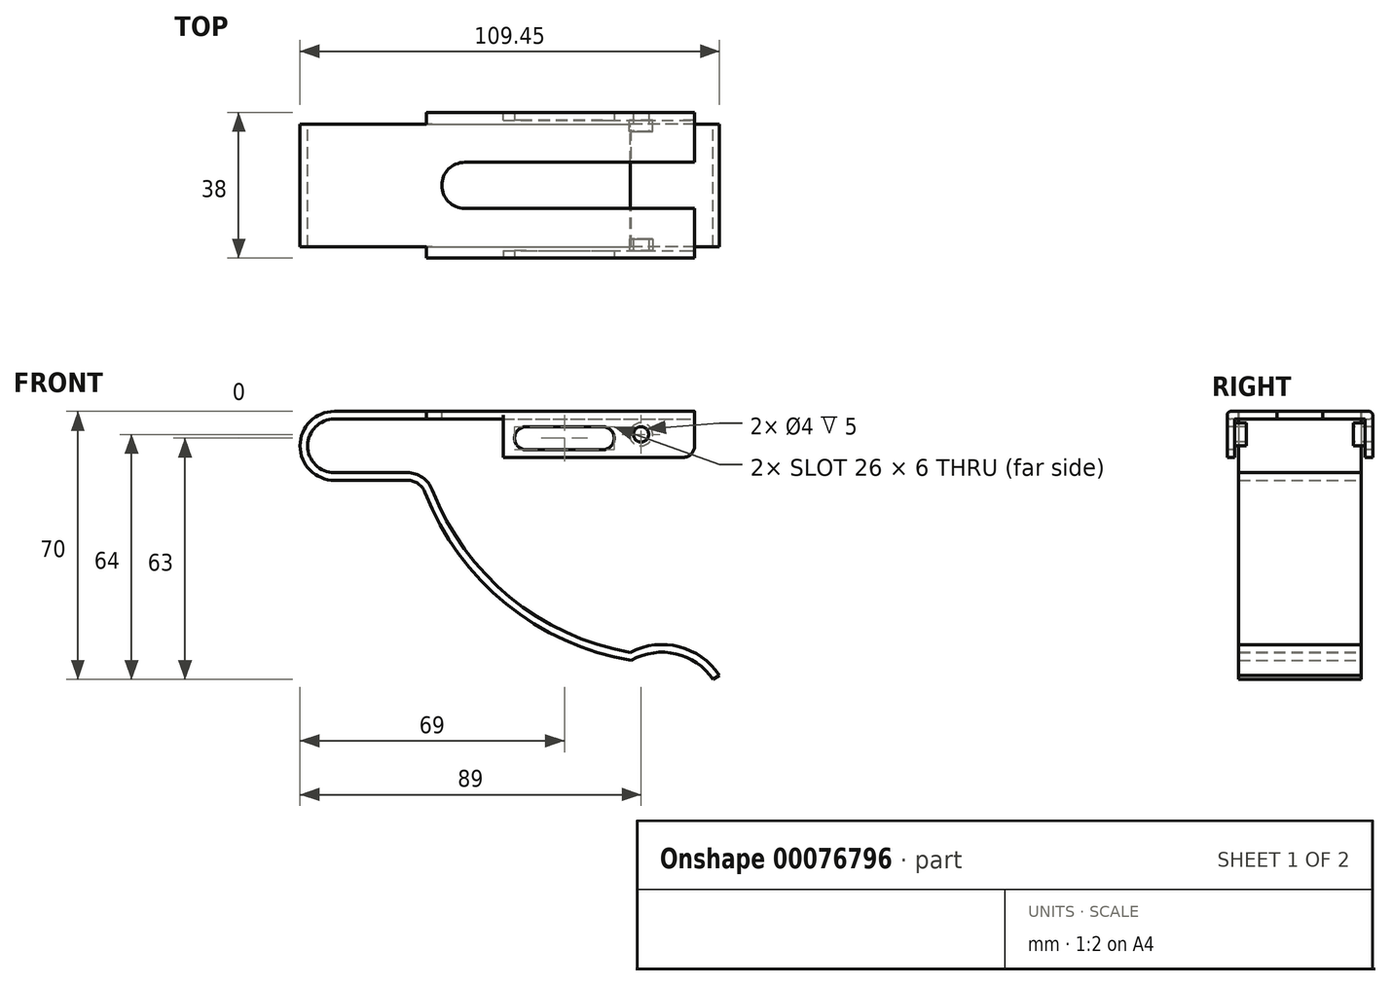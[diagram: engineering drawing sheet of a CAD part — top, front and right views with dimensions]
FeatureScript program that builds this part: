
annotation { "Feature Type Name" : "Feature", "Feature Type Description" : "" }
export const myFeature = defineFeature(function(context is Context, id is Id, definition is map)
    precondition{}
    {
        {
            var Q0;
            Q0=qCreatedBy(makeId("Front.planeOp"),FACE);
            var sketch = newSketch(context, id + "F0", { "sketchPlane" : qUnion([Q0])});
            skArc(sketch, "E0", {"start": v(0, 9) * mm, "mid": v(-9, 0) * mm, "end": v(0, -9) * mm});
            skLineSegment(sketch, "E1", {"start": v(0, 9) * mm, "end": v(94, 9) * mm});
            skLineSegment(sketch, "E2", {"start": v(0, -9) * mm, "end": v(19, -9) * mm});
            skArc(sketch, "E3", {"start": v(23.66, -12.2) * mm, "mid": v(44.77, -41.24) * mm, "end": v(77.5, -56) * mm});
            skArc(sketch, "E4", {"start": v(98.78, -61) * mm, "mid": v(89.13, -54.3) * mm, "end": v(77.5, -56) * mm});
            skPoint(sketch, "E5.visualSharp", {"position": v(22.52, -9) * mm});
            skArc(sketch, "E5.filletArc", {"start": v(23.66, -12.2) * mm, "mid": v(21.83, -9.88) * mm, "end": v(19, -9) * mm});
            skLineSegment(sketch, "E6.0", {"start": v(0, 7) * mm, "end": v(94, 7) * mm});
            skArc(sketch, "E6.1", {"start": v(0, 7) * mm, "mid": v(-7, 0) * mm, "end": v(0, -7) * mm});
            skArc(sketch, "E6.2", {"start": v(100.45, -59.9) * mm, "mid": v(89.94, -52.44) * mm, "end": v(77.15, -53.91) * mm});
            skArc(sketch, "E6.3", {"start": v(25.53, -11.47) * mm, "mid": v(45.77, -39.47) * mm, "end": v(77.15, -53.91) * mm});
            skArc(sketch, "E6.4", {"start": v(25.53, -11.47) * mm, "mid": v(22.96, -8.23) * mm, "end": v(19, -7) * mm});
            skLineSegment(sketch, "E6.5", {"start": v(0, -7) * mm, "end": v(19, -7) * mm});
            skLineSegment(sketch, "E7", {"start": v(94, 9) * mm, "end": v(94, 7) * mm});
            skLineSegment(sketch, "E8", {"start": v(100.45, -59.9) * mm, "end": v(98.78, -61) * mm});
            skSolve(sketch);
        }
        {
            var Q0;
            Q0 = qSketchRegion(id + "F0", true);
            extrude(context, id + "F1", {"entities" : qUnion([Q0]), "depth" : 16 * mm});
        }
        {
            var Q0;
            Q0=makeQuery(id+"F1.opExtrude","SWEPT_FACE",FACE,{"disambiguationData":[OSD([sQuery(id+"F0.wireOp",EDGE,"E1")])]});
            var sketch = newSketch(context, id + "F2", { "sketchPlane" : qUnion([Q0])});
            skLineSegment(sketch, "E9.bottom", {"start": v(79.88, -16) * mm, "end": v(24, -16) * mm});
            skLineSegment(sketch, "E9.top", {"start": v(94, -19) * mm, "end": v(24, -19) * mm});
            skLineSegment(sketch, "E9.left", {"start": v(94, -16) * mm, "end": v(94, -19) * mm});
            skLineSegment(sketch, "E9.right", {"start": v(24, -16) * mm, "end": v(24, -19) * mm});
            skLineSegment(sketch, "E10.top", {"start": v(94, -10.87) * mm, "end": v(79.88, -10.87) * mm});
            skLineSegment(sketch, "E10.left", {"start": v(94, -16) * mm, "end": v(94, -10.87) * mm});
            skLineSegment(sketch, "E10.right", {"start": v(79.88, -16) * mm, "end": v(79.88, -10.87) * mm});
            skSolve(sketch);
        }
        {
            var Q0;
            Q0=makeQuery(id+"F2.imprint","IMPRINT",FACE,{"disambiguationData":[TD([[makeQuery(id+"F2.imprint","IMPRINT",EDGE,{"derivedFrom":sQuery(id+"F2.wireOp",EDGE,"E10.top")}),1.0]])]});
            var Q1;
            {var subQ1=sQuery(id+"F2.wireOp",EDGE,"E9.bottom");Q1=makeQuery(id+"F2.imprint","IMPRINT",FACE,{"disambiguationData":[TD([[makeQuery(id+"F2.imprint","IMPRINT",EDGE,{"derivedFrom":subQ1}),-1.0]])]});}
            extrude(context, id + "F3", {"entities" : qUnion([Q0, Q1]), "operationType" : NewBodyOperationType.ADD, "oppositeDirection" : true, "depth" : 2 * mm});
        }
        {
            var Q0;
            Q0=makeQuery(id+"F3.opExtrude","SWEPT_FACE",FACE,{"disambiguationData":[OSD([sQuery(id+"F2.wireOp",EDGE,"E9.top")])]});
            var sketch = newSketch(context, id + "F4", { "sketchPlane" : qUnion([Q0])});
            skPoint(sketch, "E11", {"position": v(94, -3) * mm});
            skPoint(sketch, "E11.positionSnap0", {"position": v(94, 8) * mm});
            skPoint(sketch, "E12", {"position": v(94, 9) * mm});
            skLineSegment(sketch, "E13.bottom", {"start": v(44, 9) * mm, "end": v(94, 9) * mm});
            skLineSegment(sketch, "E13.top", {"start": v(44, -3) * mm, "end": v(94, -3) * mm});
            skLineSegment(sketch, "E13.left", {"start": v(44, 9) * mm, "end": v(44, -3) * mm});
            skLineSegment(sketch, "E13.right", {"start": v(94, 9) * mm, "end": v(94, -3) * mm});
            skSolve(sketch);
        }
        {
            var Q0;
            Q0 = qSketchRegion(id + "F4", true);
            extrude(context, id + "F5", {"entities" : qUnion([Q0]), "operationType" : NewBodyOperationType.ADD, "oppositeDirection" : true, "depth" : 2 * mm});
        }
        {
            var Q0;
            Q0=makeQuery(id+"F3.opExtrude","CAP_EDGE",EDGE,{"disambiguationData":[OSD([sQuery(id+"F2.wireOp",EDGE,"E9.top")])],"isStart":true});
            var Q1;
            Q1=makeQuery(id+"F3.opExtrude","CAP_EDGE",EDGE,{"disambiguationData":[OSD([sQuery(id+"F2.wireOp",EDGE,"E9.top")])],"isStart":false});
            fillet(context, id + "F6", {"entities" : qUnion([Q0, Q1]), "radius" : 1 * mm, "tangentPropagation" : true, "allowEdgeOverflow" : false});
        }
        {
            var Q0;
            Q0=makeQuery(id+"F1.opExtrude","SWEPT_BODY",BODY,{"disambiguationData":[OSD([sQuery(id+"F0.wireOp",EDGE,"E0"),sQuery(id+"F0.wireOp",EDGE,"E1"),sQuery(id+"F0.wireOp",EDGE,"E2"),sQuery(id+"F0.wireOp",EDGE,"E3"),sQuery(id+"F0.wireOp",EDGE,"E4"),sQuery(id+"F0.wireOp",EDGE,"E5.filletArc"),sQuery(id+"F0.wireOp",EDGE,"E6.0"),sQuery(id+"F0.wireOp",EDGE,"E6.1"),sQuery(id+"F0.wireOp",EDGE,"E6.2"),sQuery(id+"F0.wireOp",EDGE,"E6.3"),sQuery(id+"F0.wireOp",EDGE,"E6.4"),sQuery(id+"F0.wireOp",EDGE,"E6.5"),sQuery(id+"F0.wireOp",EDGE,"E7"),sQuery(id+"F0.wireOp",EDGE,"E8")])]});
            var Q1;
            Q1=qCreatedBy(makeId("Front.planeOp"),FACE);
            mirror(context, id + "F7", {"operationType" : NewBodyOperationType.ADD, "entities" : qUnion([Q0]), "mirrorPlane" : qUnion([Q1])});
        }
        {
            var Q0;
            {var subQ0=makeQuery(id+"F3.boolean.opBoolean","MERGE",FACE,{"derivedFrom":[makeQuery(id+"F1.opExtrude","SWEPT_FACE",FACE,{"disambiguationData":[OSD([sQuery(id+"F0.wireOp",EDGE,"E1")])]}),makeQuery(id+"F3.opExtrude","CAP_FACE",FACE,{"disambiguationData":[OSD([sQuery(id+"F2.wireOp",EDGE,"E9.bottom"),sQuery(id+"F2.wireOp",EDGE,"E9.top"),sQuery(id+"F2.wireOp",EDGE,"E9.left"),sQuery(id+"F2.wireOp",EDGE,"E9.right"),sQuery(id+"F2.wireOp",EDGE,"E10.top"),sQuery(id+"F2.wireOp",EDGE,"E10.left"),sQuery(id+"F2.wireOp",EDGE,"E10.right")])],"isStart":true})]});Q0=makeQuery(id+"F7.boolean.opBoolean","MERGE",FACE,{"derivedFrom":[subQ0,makeQuery(id+"F7.opPattern","COPY",FACE,{"derivedFrom":subQ0,"instanceName":"1"})]});}
            var sketch = newSketch(context, id + "F8", { "sketchPlane" : qUnion([Q0])});
            skPoint(sketch, "E14", {"position": v(0, 0) * mm});
            skArc(sketch, "E15", {"start": v(34, 6) * mm, "mid": v(28, 0) * mm, "end": v(34, -6) * mm});
            skPoint(sketch, "E16", {"position": v(34, 6) * mm});
            skLineSegment(sketch, "E17", {"start": v(34, 6) * mm, "end": v(94, 6) * mm});
            skPoint(sketch, "E18", {"position": v(34, -6) * mm});
            skLineSegment(sketch, "E19", {"start": v(94, 6) * mm, "end": v(94, -6) * mm});
            skLineSegment(sketch, "E20", {"start": v(94, -6) * mm, "end": v(34, -6) * mm});
            skSolve(sketch);
        }
        {
            var Q0;
            Q0 = qSketchRegion(id + "F8", true);
            extrude(context, id + "F9", {"entities" : qUnion([Q0]), "operationType" : NewBodyOperationType.REMOVE, "oppositeDirection" : true, "depth" : 2 * mm});
        }
        {
            var Q0;
            Q0=makeQuery(id+"F5.boolean.opBoolean","MERGE",FACE,{"derivedFrom":[makeQuery(id+"F3.opExtrude","SWEPT_FACE",FACE,{"disambiguationData":[OSD([sQuery(id+"F2.wireOp",EDGE,"E9.top")])]}),makeQuery(id+"F5.opExtrude","CAP_FACE",FACE,{"disambiguationData":[OSD([sQuery(id+"F4.wireOp",EDGE,"E13.bottom"),sQuery(id+"F4.wireOp",EDGE,"E13.top"),sQuery(id+"F4.wireOp",EDGE,"E13.left"),sQuery(id+"F4.wireOp",EDGE,"E13.right")])],"isStart":true})]});
            var sketch = newSketch(context, id + "F10", { "sketchPlane" : qUnion([Q0])});
            skLineSegment(sketch, "E21", {"start": v(50, 2) * mm, "end": v(70, 2) * mm});
            skArc(sketch, "E22.0.startCap", {"start": v(50, -1) * mm, "mid": v(47, 2) * mm, "end": v(50, 5) * mm});
            skArc(sketch, "E22.0.endCap", {"start": v(70, 5) * mm, "mid": v(73, 2) * mm, "end": v(70, -1) * mm});
            skLineSegment(sketch, "E22.0.left", {"start": v(50, 5) * mm, "end": v(70, 5) * mm});
            skLineSegment(sketch, "E22.0.right", {"start": v(50, -1) * mm, "end": v(70, -1) * mm});
            skSolve(sketch);
        }
        {
            var Q0;
            Q0 = qSketchRegion(id + "F10", true);
            extrude(context, id + "F11", {"entities" : qUnion([Q0]), "operationType" : NewBodyOperationType.ADD, "endBound" : BoundingType.THROUGH_ALL, "depth" : 25 * mm});
        }
        {
            var Q0;
            Q0=makeQuery(id+"F5.boolean.opBoolean","MERGE",FACE,{"derivedFrom":[makeQuery(id+"F3.opExtrude","SWEPT_FACE",FACE,{"disambiguationData":[OSD([sQuery(id+"F2.wireOp",EDGE,"E9.top")])]}),makeQuery(id+"F5.opExtrude","CAP_FACE",FACE,{"disambiguationData":[OSD([sQuery(id+"F4.wireOp",EDGE,"E13.bottom"),sQuery(id+"F4.wireOp",EDGE,"E13.top"),sQuery(id+"F4.wireOp",EDGE,"E13.left"),sQuery(id+"F4.wireOp",EDGE,"E13.right")])],"isStart":true})]});
            var sketch = newSketch(context, id + "F12", { "sketchPlane" : qUnion([Q0])});
            skPoint(sketch, "E23", {"position": v(80, 3) * mm});
            skPoint(sketch, "E23.positionSnap0", {"position": v(94, 2.5) * mm});
            skSolve(sketch);
        }
        {
            var Q0;
            Q0=sQuery(id+"F12.wireOp",VERTEX,"E23");
            var Q1;
            Q1=makeQuery(id+"F1.opExtrude","SWEPT_BODY",BODY,{"disambiguationData":[OSD([sQuery(id+"F0.wireOp",EDGE,"E0"),sQuery(id+"F0.wireOp",EDGE,"E1"),sQuery(id+"F0.wireOp",EDGE,"E2"),sQuery(id+"F0.wireOp",EDGE,"E3"),sQuery(id+"F0.wireOp",EDGE,"E4"),sQuery(id+"F0.wireOp",EDGE,"E5.filletArc"),sQuery(id+"F0.wireOp",EDGE,"E6.0"),sQuery(id+"F0.wireOp",EDGE,"E6.1"),sQuery(id+"F0.wireOp",EDGE,"E6.2"),sQuery(id+"F0.wireOp",EDGE,"E6.3"),sQuery(id+"F0.wireOp",EDGE,"E6.4"),sQuery(id+"F0.wireOp",EDGE,"E6.5"),sQuery(id+"F0.wireOp",EDGE,"E7"),sQuery(id+"F0.wireOp",EDGE,"E8")])]});
            hole(context, id + "F13", {"style" : HoleStyle.SIMPLE, "endStyle" : HoleEndStyle.THROUGH, "holeDiameter" : 4 * mm, "locations" : qUnion([Q0]), "scope" : qUnion([Q1]), "isTappedThrough" : true});
        }
        {
            var Q0;
            Q0=makeQuery(id+"F5.boolean.opBoolean","MERGE",FACE,{"derivedFrom":[makeQuery(id+"F3.opExtrude","SWEPT_FACE",FACE,{"disambiguationData":[OSD([sQuery(id+"F2.wireOp",EDGE,"E9.top")])]}),makeQuery(id+"F5.opExtrude","CAP_FACE",FACE,{"disambiguationData":[OSD([sQuery(id+"F4.wireOp",EDGE,"E13.bottom"),sQuery(id+"F4.wireOp",EDGE,"E13.top"),sQuery(id+"F4.wireOp",EDGE,"E13.left"),sQuery(id+"F4.wireOp",EDGE,"E13.right")])],"isStart":true})]});
            var sketch = newSketch(context, id + "F14", { "sketchPlane" : qUnion([Q0])});
            skCircle(sketch, "E24.0", {"center": v(80, 3) * mm, "radius": 2 * mm});
            skCircle(sketch, "E25.0", {"center": v(80, 3) * mm, "radius": 3 * mm});
            skSolve(sketch);
        }
        {
            var Q0;
            Q0 = qSketchRegion(id + "F14", true);
            extrude(context, id + "F15", {"entities" : qUnion([Q0]), "operationType" : NewBodyOperationType.ADD, "oppositeDirection" : true, "depth" : 5 * mm});
        }
        {
            var Q0;
            Q0=makeQuery(id+"F11.opExtrude","CAP_FACE",FACE,{"disambiguationData":[OSD([sQuery(id+"F10.wireOp",EDGE,"E22.0.startCap"),sQuery(id+"F10.wireOp",EDGE,"E22.0.endCap"),sQuery(id+"F10.wireOp",EDGE,"E22.0.left"),sQuery(id+"F10.wireOp",EDGE,"E22.0.right")])],"isStart":false});
            extrude(context, id + "F16", {"entities" : qUnion([Q0]), "operationType" : NewBodyOperationType.REMOVE, "endBound" : BoundingType.THROUGH_ALL, "oppositeDirection" : true, "depth" : 25 * mm});
        }
        {
            var Q0;
            Q0=makeQuery(id+"F7.opPattern","COPY",FACE,{"derivedFrom":makeQuery(id+"F5.boolean.opBoolean","MERGE",FACE,{"derivedFrom":[makeQuery(id+"F3.opExtrude","SWEPT_FACE",FACE,{"disambiguationData":[OSD([sQuery(id+"F2.wireOp",EDGE,"E9.top")])]}),makeQuery(id+"F5.opExtrude","CAP_FACE",FACE,{"disambiguationData":[OSD([sQuery(id+"F4.wireOp",EDGE,"E13.bottom"),sQuery(id+"F4.wireOp",EDGE,"E13.top"),sQuery(id+"F4.wireOp",EDGE,"E13.left"),sQuery(id+"F4.wireOp",EDGE,"E13.right")])],"isStart":true})]}),"instanceName":"1"});
            var sketch = newSketch(context, id + "F17", { "sketchPlane" : qUnion([Q0])});
            skCircle(sketch, "E26.0", {"center": v(-80, 3) * mm, "radius": 3 * mm});
            skSolve(sketch);
        }
        {
            var Q0;
            Q0=makeQuery(id+"F17.imprint","IMPRINT",FACE,{"disambiguationData":[TD([[makeQuery(id+"F17.imprint","IMPRINT",EDGE,{"derivedFrom":sQuery(id+"F17.wireOp",EDGE,"E26.0")}),1.0]])]});
            extrude(context, id + "F18", {"entities" : qUnion([Q0]), "operationType" : NewBodyOperationType.ADD, "oppositeDirection" : true, "depth" : 5 * mm});
        }
        {
            var Q0;
            Q0=makeQuery(id+"F5.opExtrude","SWEPT_EDGE",EDGE,{"disambiguationData":[OSD([sQuery(id+"F4.wireOp",EDGE,"E13.top"),sQuery(id+"F4.wireOp",EDGE,"E13.right")])]});
            var Q1;
            Q1=makeQuery(id+"F7.opPattern","COPY",EDGE,{"derivedFrom":makeQuery(id+"F5.opExtrude","SWEPT_EDGE",EDGE,{"disambiguationData":[OSD([sQuery(id+"F4.wireOp",EDGE,"E13.top"),sQuery(id+"F4.wireOp",EDGE,"E13.right")])]}),"instanceName":"1"});
            fillet(context, id + "F19", {"entities" : qUnion([Q0, Q1]), "radius" : 3 * mm, "tangentPropagation" : true, "allowEdgeOverflow" : false});
        }
    });
